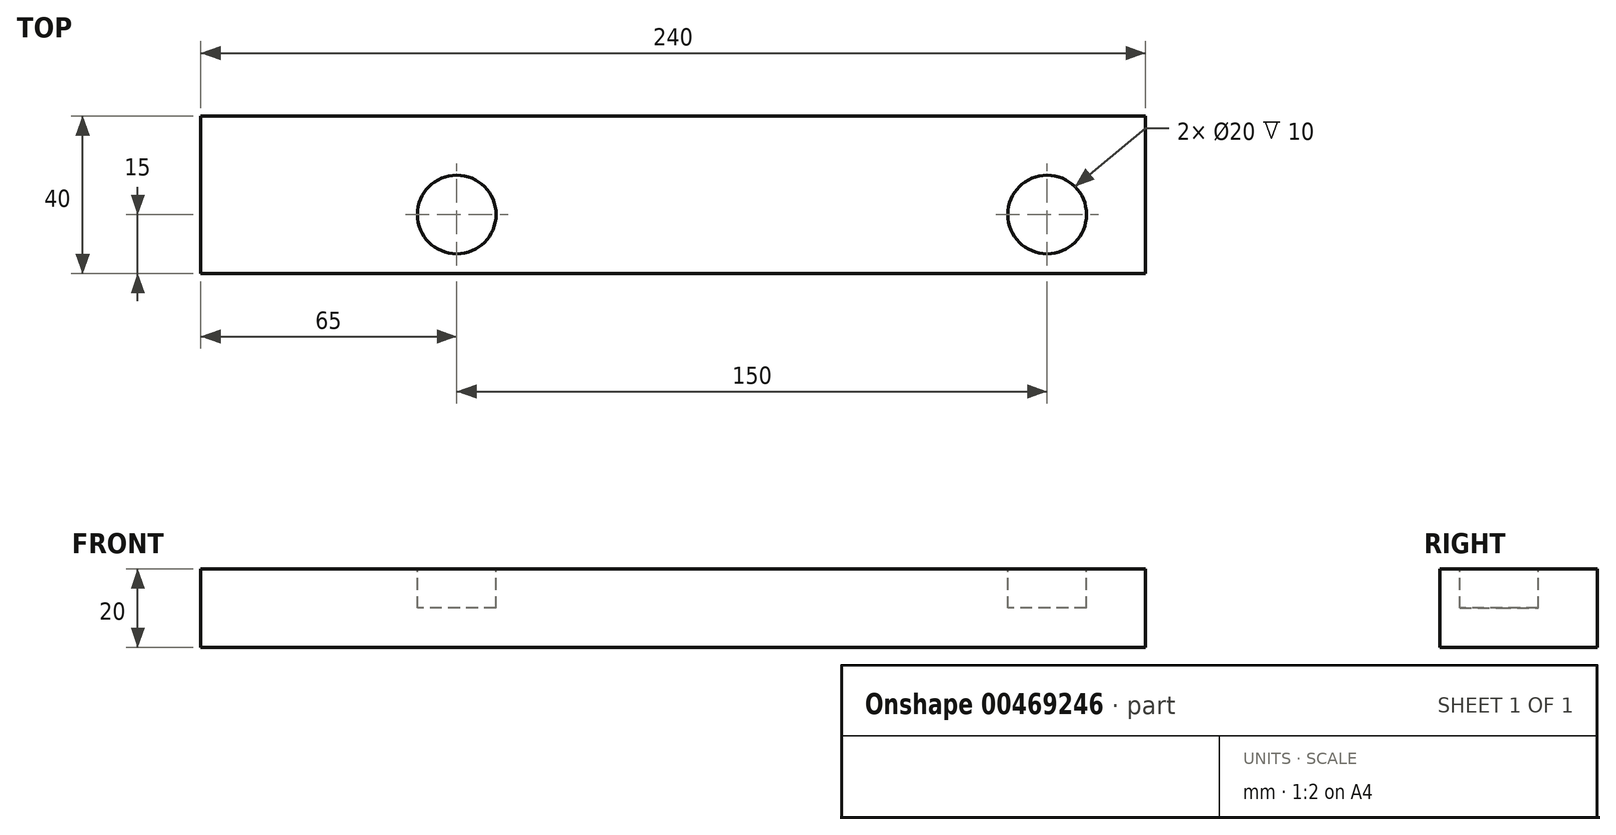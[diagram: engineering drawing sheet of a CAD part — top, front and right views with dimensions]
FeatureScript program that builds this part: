
annotation { "Feature Type Name" : "Feature", "Feature Type Description" : "" }
export const myFeature = defineFeature(function(context is Context, id is Id, definition is map)
    precondition{}
    {
        {
            var Q0;
            Q0=qCreatedBy(makeId("Top.planeOp"),FACE);
            var sketch = newSketch(context, id + "F0", { "sketchPlane" : qUnion([Q0])});
            skLineSegment(sketch, "E0.bottom", {"start": v(-120, -20) * mm, "end": v(120, -20) * mm});
            skLineSegment(sketch, "E0.top", {"start": v(-120, 20) * mm, "end": v(120, 20) * mm});
            skLineSegment(sketch, "E0.left", {"start": v(-120, -20) * mm, "end": v(-120, 20) * mm});
            skLineSegment(sketch, "E0.right", {"start": v(120, -20) * mm, "end": v(120, 20) * mm});
            skPoint(sketch, "E0.middle", {"position": v(0, 0) * mm});
            skSolve(sketch);
        }
        {
            var Q0;
            Q0 = qSketchRegion(id + "F0", true);
            extrude(context, id + "F1", {"entities" : qUnion([Q0]), "endBound" : BoundingType.SYMMETRIC, "depth" : 20 * mm});
        }
        {
            var Q0;
            Q0=makeQuery(id+"F1.opExtrude","CAP_FACE",FACE,{"disambiguationData":[OSD([sQuery(id+"F0.wireOp",EDGE,"E0.bottom"),sQuery(id+"F0.wireOp",EDGE,"E0.top"),sQuery(id+"F0.wireOp",EDGE,"E0.left"),sQuery(id+"F0.wireOp",EDGE,"E0.right")])],"isStart":false});
            var sketch = newSketch(context, id + "F2", { "sketchPlane" : qUnion([Q0])});
            skCircle(sketch, "E1", {"center": v(-55, -5) * mm, "radius": 10 * mm});
            skCircle(sketch, "E2", {"center": v(95, -5) * mm, "radius": 10 * mm});
            skSolve(sketch);
        }
        {
            var Q0;
            Q0 = qSketchRegion(id + "F2", true);
            extrude(context, id + "F3", {"entities" : qUnion([Q0]), "operationType" : NewBodyOperationType.REMOVE, "oppositeDirection" : true, "depth" : 10 * mm});
        }
    });
